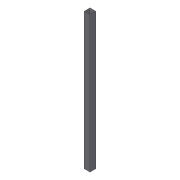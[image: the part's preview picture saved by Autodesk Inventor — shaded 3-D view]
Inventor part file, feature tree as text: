
AUTODESK INVENTOR PART (.ipt)
format: ipt  version: 2012 (Build 160160000, 160)  size: 73,216 bytes
history: native  units: in
note: dims shown in document units (in); Inventor stores cm internally (conversion verified against a paired STEP export)
features: extrude x1, shell x1, sketch x1
ambient origin geometry x8: Origin, YZ Plane, XZ Plane, XY Plane, X Axis, Y Axis, Z Axis, Center Point
bodies: Solid1 (feature_tree)
feature tree (3):
  extrude  "Extrusion1"  Depth=1.0in TaperAngle=0.0deg
  shell  "Shell2"  Thickness=1.0in
  sketch  "Sketch1"  dims[d1=21.0in d6=1.0in d7=0.0in d9=1.0in d10=0.0625in]
